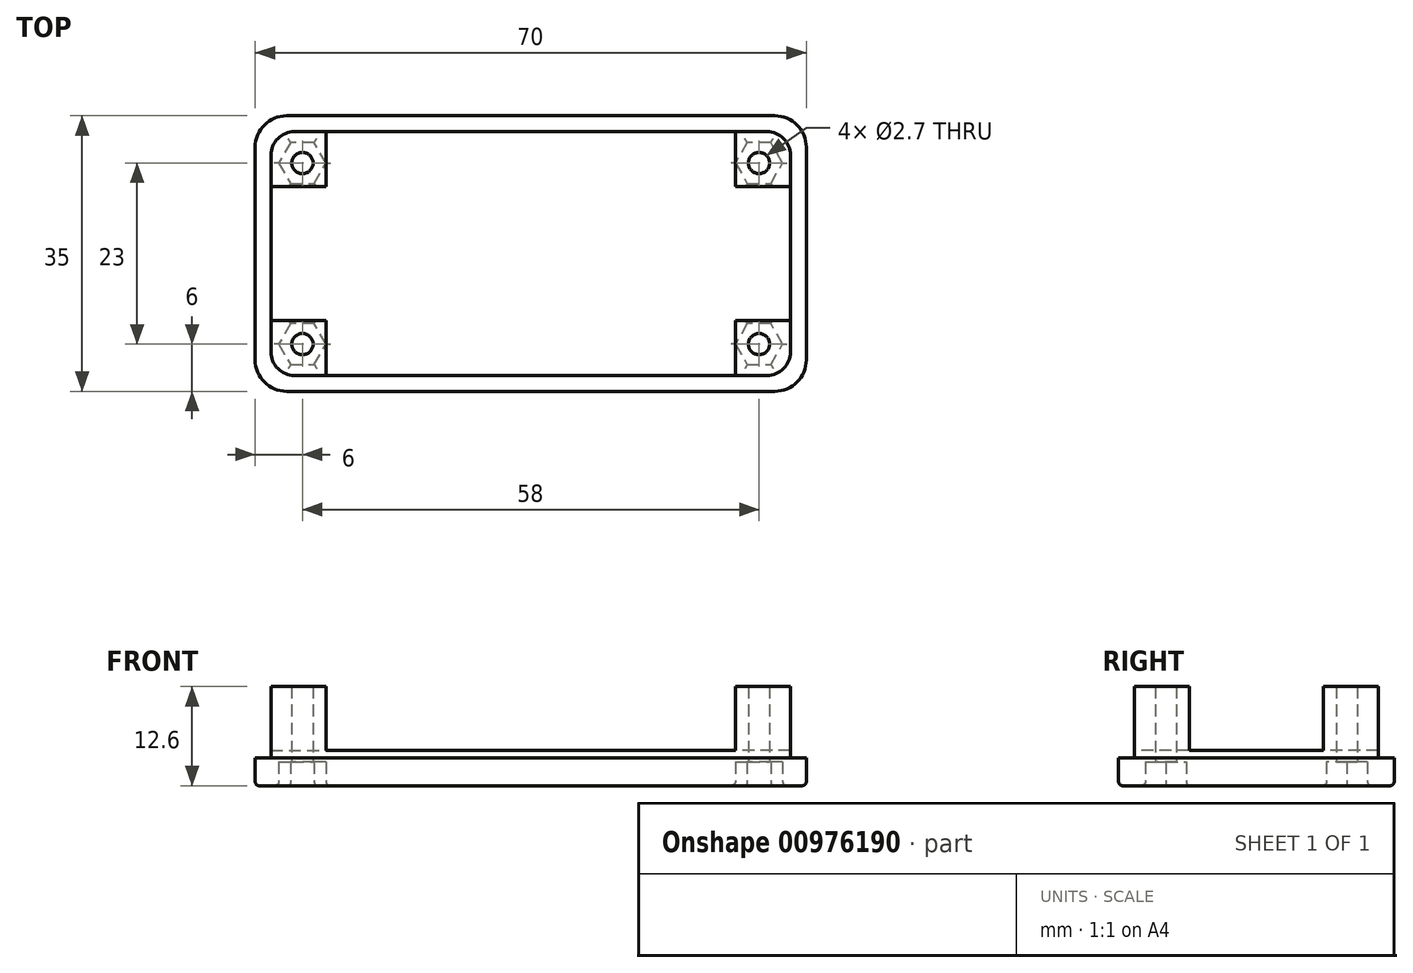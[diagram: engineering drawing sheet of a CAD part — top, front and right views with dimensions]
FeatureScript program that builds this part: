
annotation { "Feature Type Name" : "Feature", "Feature Type Description" : "" }
export const myFeature = defineFeature(function(context is Context, id is Id, definition is map)
    precondition{}
    {
        {
            var Q0;
            Q0=qCreatedBy(makeId("Top.planeOp"),FACE);
            var sketch = newSketch(context, id + "F0", { "sketchPlane" : qUnion([Q0])});
            skLineSegment(sketch, "E0.bottom", {"start": v(-31, 17.5) * mm, "end": v(31, 17.5) * mm});
            skLineSegment(sketch, "E0.top", {"start": v(-31, -17.5) * mm, "end": v(31, -17.5) * mm});
            skLineSegment(sketch, "E0.left", {"start": v(-35, 13.5) * mm, "end": v(-35, -13.5) * mm});
            skLineSegment(sketch, "E0.right", {"start": v(35, 13.5) * mm, "end": v(35, -13.5) * mm});
            skPoint(sketch, "E1.visualSharp", {"position": v(-35, 17.5) * mm});
            skArc(sketch, "E1.filletArc", {"start": v(-31, 17.5) * mm, "mid": v(-33.83, 16.33) * mm, "end": v(-35, 13.5) * mm});
            skPoint(sketch, "E2.visualSharp", {"position": v(-35, -17.5) * mm});
            skArc(sketch, "E2.filletArc", {"start": v(-35, -13.5) * mm, "mid": v(-33.83, -16.33) * mm, "end": v(-31, -17.5) * mm});
            skPoint(sketch, "E3.visualSharp", {"position": v(35, -17.5) * mm});
            skArc(sketch, "E3.filletArc", {"start": v(31, -17.5) * mm, "mid": v(33.83, -16.33) * mm, "end": v(35, -13.5) * mm});
            skPoint(sketch, "E4.visualSharp", {"position": v(35, 17.5) * mm});
            skArc(sketch, "E4.filletArc", {"start": v(35, 13.5) * mm, "mid": v(33.83, 16.33) * mm, "end": v(31, 17.5) * mm});
            skSolve(sketch);
        }
        {
            var Q0;
            Q0=makeQuery(id+"F0.imprint","IMPRINT",FACE,{"disambiguationData":[TD([[makeQuery(id+"F0.imprint","IMPRINT",EDGE,{"derivedFrom":sQuery(id+"F0.wireOp",EDGE,"E0.bottom")}),-1.0]])]});
            extrude(context, id + "F1", {"entities" : qUnion([Q0]), "depth" : 3.5 * mm, "offsetDistance" : 25 * mm});
        }
        {
            var Q0;
            Q0=makeQuery(id+"F1.opExtrude","CAP_FACE",FACE,{"disambiguationData":[OSD([sQuery(id+"F0.wireOp",EDGE,"E0.bottom"),sQuery(id+"F0.wireOp",EDGE,"E0.top"),sQuery(id+"F0.wireOp",EDGE,"E0.left"),sQuery(id+"F0.wireOp",EDGE,"E0.right"),sQuery(id+"F0.wireOp",EDGE,"E1.filletArc"),sQuery(id+"F0.wireOp",EDGE,"E2.filletArc"),sQuery(id+"F0.wireOp",EDGE,"E3.filletArc"),sQuery(id+"F0.wireOp",EDGE,"E4.filletArc")])],"isStart":false});
            var sketch = newSketch(context, id + "F2", { "sketchPlane" : qUnion([Q0])});
            skLineSegment(sketch, "E5.bottom", {"start": v(-30, 15.5) * mm, "end": v(30, 15.5) * mm});
            skLineSegment(sketch, "E5.top", {"start": v(-30, -15.5) * mm, "end": v(30, -15.5) * mm});
            skLineSegment(sketch, "E5.left", {"start": v(-33, 12.5) * mm, "end": v(-33, -12.5) * mm});
            skLineSegment(sketch, "E5.right", {"start": v(33, 12.5) * mm, "end": v(33, -12.5) * mm});
            skPoint(sketch, "E6.visualSharp", {"position": v(-33, 15.5) * mm});
            skArc(sketch, "E6.filletArc", {"start": v(-30, 15.5) * mm, "mid": v(-32.12, 14.62) * mm, "end": v(-33, 12.5) * mm});
            skPoint(sketch, "E7.visualSharp", {"position": v(-33, -15.5) * mm});
            skArc(sketch, "E7.filletArc", {"start": v(-33, -12.5) * mm, "mid": v(-32.12, -14.62) * mm, "end": v(-30, -15.5) * mm});
            skPoint(sketch, "E8.visualSharp", {"position": v(33, -15.5) * mm});
            skArc(sketch, "E8.filletArc", {"start": v(30, -15.5) * mm, "mid": v(32.12, -14.62) * mm, "end": v(33, -12.5) * mm});
            skPoint(sketch, "E9.visualSharp", {"position": v(33, 15.5) * mm});
            skArc(sketch, "E9.filletArc", {"start": v(33, 12.5) * mm, "mid": v(32.12, 14.62) * mm, "end": v(30, 15.5) * mm});
            skSolve(sketch);
        }
        {
            var Q0;
            Q0=qSketchRegion(id+"F2",true);
            extrude(context, id + "F3", {"entities" : qUnion([Q0]), "operationType" : NewBodyOperationType.ADD, "depth" : 1 * mm, "offsetDistance" : 25 * mm});
        }
        {
            var Q0;
            Q0=makeQuery(id+"F3.opExtrude","CAP_FACE",FACE,{"disambiguationData":[OSD([sQuery(id+"F2.wireOp",EDGE,"E5.bottom"),sQuery(id+"F2.wireOp",EDGE,"E5.top"),sQuery(id+"F2.wireOp",EDGE,"E5.left"),sQuery(id+"F2.wireOp",EDGE,"E5.right"),sQuery(id+"F2.wireOp",EDGE,"E6.filletArc"),sQuery(id+"F2.wireOp",EDGE,"E7.filletArc"),sQuery(id+"F2.wireOp",EDGE,"E8.filletArc"),sQuery(id+"F2.wireOp",EDGE,"E9.filletArc")])],"isStart":false});
            var sketch = newSketch(context, id + "F4", { "sketchPlane" : qUnion([Q0])});
            skLineSegment(sketch, "E10.bottom", {"start": v(-30, 15.5) * mm, "end": v(-26, 15.5) * mm});
            skLineSegment(sketch, "E10.top", {"start": v(-33, 8.5) * mm, "end": v(-26, 8.5) * mm});
            skLineSegment(sketch, "E10.left", {"start": v(-33, 12.5) * mm, "end": v(-33, 8.5) * mm});
            skLineSegment(sketch, "E10.right", {"start": v(-26, 15.5) * mm, "end": v(-26, 8.5) * mm});
            skLineSegment(sketch, "E11.bottom", {"start": v(-33, -8.5) * mm, "end": v(-26, -8.5) * mm});
            skLineSegment(sketch, "E11.top", {"start": v(-30, -15.5) * mm, "end": v(-26, -15.5) * mm});
            skLineSegment(sketch, "E11.left", {"start": v(-33, -8.5) * mm, "end": v(-33, -12.5) * mm});
            skLineSegment(sketch, "E11.right", {"start": v(-26, -8.5) * mm, "end": v(-26, -15.5) * mm});
            skLineSegment(sketch, "E12.bottom", {"start": v(26, 15.5) * mm, "end": v(30, 15.5) * mm});
            skLineSegment(sketch, "E12.top", {"start": v(26, 8.5) * mm, "end": v(33, 8.5) * mm});
            skLineSegment(sketch, "E12.left", {"start": v(26, 15.5) * mm, "end": v(26, 8.5) * mm});
            skLineSegment(sketch, "E12.right", {"start": v(33, 12.5) * mm, "end": v(33, 8.5) * mm});
            skLineSegment(sketch, "E13.bottom", {"start": v(33, -8.5) * mm, "end": v(26, -8.5) * mm});
            skLineSegment(sketch, "E13.top", {"start": v(30, -15.5) * mm, "end": v(26, -15.5) * mm});
            skLineSegment(sketch, "E13.left", {"start": v(33, -8.5) * mm, "end": v(33, -12.5) * mm});
            skLineSegment(sketch, "E13.right", {"start": v(26, -8.5) * mm, "end": v(26, -15.5) * mm});
            skPoint(sketch, "E14.visualSharp", {"position": v(-33, 15.5) * mm});
            skArc(sketch, "E14.filletArc", {"start": v(-30, 15.5) * mm, "mid": v(-32.12, 14.62) * mm, "end": v(-33, 12.5) * mm});
            skPoint(sketch, "E15.visualSharp", {"position": v(-33, -15.5) * mm});
            skArc(sketch, "E15.filletArc", {"start": v(-33, -12.5) * mm, "mid": v(-32.12, -14.62) * mm, "end": v(-30, -15.5) * mm});
            skPoint(sketch, "E16.visualSharp", {"position": v(33, -15.5) * mm});
            skArc(sketch, "E16.filletArc", {"start": v(30, -15.5) * mm, "mid": v(32.12, -14.62) * mm, "end": v(33, -12.5) * mm});
            skPoint(sketch, "E17.visualSharp", {"position": v(33, 15.5) * mm});
            skArc(sketch, "E17.filletArc", {"start": v(33, 12.5) * mm, "mid": v(32.12, 14.62) * mm, "end": v(30, 15.5) * mm});
            skSolve(sketch);
        }
        {
            var Q0;
            Q0=qSketchRegion(id+"F4",true);
            extrude(context, id + "F5", {"entities" : qUnion([Q0]), "operationType" : NewBodyOperationType.ADD, "depth" : 8.1 * mm, "offsetDistance" : 25 * mm});
        }
        {
            var Q0;
            Q0=makeQuery(id+"F1.opExtrude","CAP_FACE",FACE,{"disambiguationData":[OSD([sQuery(id+"F0.wireOp",EDGE,"E0.bottom"),sQuery(id+"F0.wireOp",EDGE,"E0.top"),sQuery(id+"F0.wireOp",EDGE,"E0.left"),sQuery(id+"F0.wireOp",EDGE,"E0.right"),sQuery(id+"F0.wireOp",EDGE,"E1.filletArc"),sQuery(id+"F0.wireOp",EDGE,"E2.filletArc"),sQuery(id+"F0.wireOp",EDGE,"E3.filletArc"),sQuery(id+"F0.wireOp",EDGE,"E4.filletArc")])],"isStart":true});
            var sketch = newSketch(context, id + "F6", { "sketchPlane" : qUnion([Q0])});
            skPoint(sketch, "E18", {"position": v(-29, 11.5) * mm});
            skPoint(sketch, "E19", {"position": v(-29, -11.5) * mm});
            skPoint(sketch, "E20", {"position": v(29, -11.5) * mm});
            skPoint(sketch, "E21", {"position": v(29, 11.5) * mm});
            skCircle(sketch, "E22.cCircle", {"center": v(-29, 11.5) * mm, "radius": 2.6 * mm, "construction": true});
            skLineSegment(sketch, "E22.0", {"start": v(-27.5, 8.9) * mm, "end": v(-30.5, 8.9) * mm});
            skLineSegment(sketch, "E22.1", {"start": v(-30.5, 8.9) * mm, "end": v(-32, 11.5) * mm});
            skLineSegment(sketch, "E22.2", {"start": v(-32, 11.5) * mm, "end": v(-30.5, 14.1) * mm});
            skLineSegment(sketch, "E22.3", {"start": v(-30.5, 14.1) * mm, "end": v(-27.5, 14.1) * mm});
            skLineSegment(sketch, "E22.4", {"start": v(-27.5, 14.1) * mm, "end": v(-26, 11.5) * mm});
            skLineSegment(sketch, "E22.5", {"start": v(-26, 11.5) * mm, "end": v(-27.5, 8.9) * mm});
            skPoint(sketch, "E22.0.midPoint", {"position": v(-29, 8.9) * mm});
            skCircle(sketch, "E23.cCircle", {"center": v(29, 11.5) * mm, "radius": 2.6 * mm, "construction": true});
            skLineSegment(sketch, "E23.0", {"start": v(30.5, 8.9) * mm, "end": v(27.5, 8.9) * mm});
            skLineSegment(sketch, "E23.1", {"start": v(27.5, 8.9) * mm, "end": v(26, 11.5) * mm});
            skLineSegment(sketch, "E23.2", {"start": v(26, 11.5) * mm, "end": v(27.5, 14.1) * mm});
            skLineSegment(sketch, "E23.3", {"start": v(27.5, 14.1) * mm, "end": v(30.5, 14.1) * mm});
            skLineSegment(sketch, "E23.4", {"start": v(30.5, 14.1) * mm, "end": v(32, 11.5) * mm});
            skLineSegment(sketch, "E23.5", {"start": v(32, 11.5) * mm, "end": v(30.5, 8.9) * mm});
            skPoint(sketch, "E23.0.midPoint", {"position": v(29, 8.9) * mm});
            skCircle(sketch, "E24.cCircle", {"center": v(29, -11.5) * mm, "radius": 2.6 * mm, "construction": true});
            skLineSegment(sketch, "E24.0", {"start": v(27.5, -8.9) * mm, "end": v(30.5, -8.9) * mm});
            skLineSegment(sketch, "E24.1", {"start": v(30.5, -8.9) * mm, "end": v(32, -11.5) * mm});
            skLineSegment(sketch, "E24.2", {"start": v(32, -11.5) * mm, "end": v(30.5, -14.1) * mm});
            skLineSegment(sketch, "E24.3", {"start": v(30.5, -14.1) * mm, "end": v(27.5, -14.1) * mm});
            skLineSegment(sketch, "E24.4", {"start": v(27.5, -14.1) * mm, "end": v(26, -11.5) * mm});
            skLineSegment(sketch, "E24.5", {"start": v(26, -11.5) * mm, "end": v(27.5, -8.9) * mm});
            skPoint(sketch, "E24.0.midPoint", {"position": v(29, -8.9) * mm});
            skCircle(sketch, "E25.cCircle", {"center": v(-29, -11.5) * mm, "radius": 2.6 * mm, "construction": true});
            skLineSegment(sketch, "E25.0", {"start": v(-30.5, -8.9) * mm, "end": v(-27.5, -8.9) * mm});
            skLineSegment(sketch, "E25.1", {"start": v(-27.5, -8.9) * mm, "end": v(-26, -11.5) * mm});
            skLineSegment(sketch, "E25.2", {"start": v(-26, -11.5) * mm, "end": v(-27.5, -14.1) * mm});
            skLineSegment(sketch, "E25.3", {"start": v(-27.5, -14.1) * mm, "end": v(-30.5, -14.1) * mm});
            skLineSegment(sketch, "E25.4", {"start": v(-30.5, -14.1) * mm, "end": v(-32, -11.5) * mm});
            skLineSegment(sketch, "E25.5", {"start": v(-32, -11.5) * mm, "end": v(-30.5, -8.9) * mm});
            skPoint(sketch, "E25.0.midPoint", {"position": v(-29, -8.9) * mm});
            skCircle(sketch, "E26", {"center": v(-29, 11.5) * mm, "radius": 1.35 * mm});
            skCircle(sketch, "E27", {"center": v(29, 11.5) * mm, "radius": 1.35 * mm});
            skCircle(sketch, "E28", {"center": v(29, -11.5) * mm, "radius": 1.35 * mm});
            skCircle(sketch, "E29", {"center": v(-29, -11.5) * mm, "radius": 1.35 * mm});
            skSolve(sketch);
        }
        {
            var Q0;
            Q0=qSketchRegion(id+"F6",true);
            extrude(context, id + "F7", {"entities" : qUnion([Q0]), "operationType" : NewBodyOperationType.REMOVE, "oppositeDirection" : true, "depth" : 3 * mm, "offsetDistance" : 25 * mm});
        }
        {
            var Q0;
            Q0=makeQuery(id+"F7.boolean.opBoolean","SPLIT",FACE,{"disambiguationData":[TD([makeQuery(id+"F7.opExtrude","SWEPT_FACE",FACE,{"disambiguationData":[OSD([sQuery(id+"F6.wireOp",EDGE,"E26")])]})])],"derivedFrom":makeQuery(id+"F1.opExtrude","CAP_FACE",FACE,{"disambiguationData":[OSD([sQuery(id+"F0.wireOp",EDGE,"E0.bottom"),sQuery(id+"F0.wireOp",EDGE,"E0.top"),sQuery(id+"F0.wireOp",EDGE,"E0.left"),sQuery(id+"F0.wireOp",EDGE,"E0.right"),sQuery(id+"F0.wireOp",EDGE,"E1.filletArc"),sQuery(id+"F0.wireOp",EDGE,"E2.filletArc"),sQuery(id+"F0.wireOp",EDGE,"E3.filletArc"),sQuery(id+"F0.wireOp",EDGE,"E4.filletArc")])],"isStart":true})});
            var Q1;
            Q1=makeQuery(id+"F7.boolean.opBoolean","SPLIT",FACE,{"disambiguationData":[TD([makeQuery(id+"F7.opExtrude","SWEPT_FACE",FACE,{"disambiguationData":[OSD([sQuery(id+"F6.wireOp",EDGE,"E27")])]})])],"derivedFrom":makeQuery(id+"F1.opExtrude","CAP_FACE",FACE,{"disambiguationData":[OSD([sQuery(id+"F0.wireOp",EDGE,"E0.bottom"),sQuery(id+"F0.wireOp",EDGE,"E0.top"),sQuery(id+"F0.wireOp",EDGE,"E0.left"),sQuery(id+"F0.wireOp",EDGE,"E0.right"),sQuery(id+"F0.wireOp",EDGE,"E1.filletArc"),sQuery(id+"F0.wireOp",EDGE,"E2.filletArc"),sQuery(id+"F0.wireOp",EDGE,"E3.filletArc"),sQuery(id+"F0.wireOp",EDGE,"E4.filletArc")])],"isStart":true})});
            var Q2;
            Q2=makeQuery(id+"F7.boolean.opBoolean","SPLIT",FACE,{"disambiguationData":[TD([makeQuery(id+"F7.opExtrude","SWEPT_FACE",FACE,{"disambiguationData":[OSD([sQuery(id+"F6.wireOp",EDGE,"E28")])]})])],"derivedFrom":makeQuery(id+"F1.opExtrude","CAP_FACE",FACE,{"disambiguationData":[OSD([sQuery(id+"F0.wireOp",EDGE,"E0.bottom"),sQuery(id+"F0.wireOp",EDGE,"E0.top"),sQuery(id+"F0.wireOp",EDGE,"E0.left"),sQuery(id+"F0.wireOp",EDGE,"E0.right"),sQuery(id+"F0.wireOp",EDGE,"E1.filletArc"),sQuery(id+"F0.wireOp",EDGE,"E2.filletArc"),sQuery(id+"F0.wireOp",EDGE,"E3.filletArc"),sQuery(id+"F0.wireOp",EDGE,"E4.filletArc")])],"isStart":true})});
            var Q3;
            Q3=makeQuery(id+"F7.boolean.opBoolean","SPLIT",FACE,{"disambiguationData":[TD([makeQuery(id+"F7.opExtrude","SWEPT_FACE",FACE,{"disambiguationData":[OSD([sQuery(id+"F6.wireOp",EDGE,"E29")])]})])],"derivedFrom":makeQuery(id+"F1.opExtrude","CAP_FACE",FACE,{"disambiguationData":[OSD([sQuery(id+"F0.wireOp",EDGE,"E0.bottom"),sQuery(id+"F0.wireOp",EDGE,"E0.top"),sQuery(id+"F0.wireOp",EDGE,"E0.left"),sQuery(id+"F0.wireOp",EDGE,"E0.right"),sQuery(id+"F0.wireOp",EDGE,"E1.filletArc"),sQuery(id+"F0.wireOp",EDGE,"E2.filletArc"),sQuery(id+"F0.wireOp",EDGE,"E3.filletArc"),sQuery(id+"F0.wireOp",EDGE,"E4.filletArc")])],"isStart":true})});
            extrude(context, id + "F8", {"entities" : qUnion([Q0, Q1, Q2, Q3]), "operationType" : NewBodyOperationType.REMOVE, "endBound" : BoundingType.THROUGH_ALL, "oppositeDirection" : true, "depth" : 25 * mm, "offsetDistance" : 25 * mm});
        }
        {
            var Q0;
            {var subQ0=sQuery(id+"F0.wireOp",EDGE,"E3.filletArc");var subQ1=sQuery(id+"F0.wireOp",EDGE,"E2.filletArc");var subQ2=sQuery(id+"F0.wireOp",EDGE,"E1.filletArc");var subQ3=sQuery(id+"F0.wireOp",EDGE,"E0.right");var subQ4=sQuery(id+"F0.wireOp",EDGE,"E0.left");var subQ5=sQuery(id+"F0.wireOp",EDGE,"E0.bottom");var subQ6=sQuery(id+"F0.wireOp",EDGE,"E0.top");var subQ7=sQuery(id+"F0.wireOp",EDGE,"E4.filletArc");Q0=makeQuery(id+"F7.boolean.opBoolean","SPLIT",FACE,{"disambiguationData":[TD([makeQuery(id+"F1.opExtrude","SWEPT_FACE",FACE,{"disambiguationData":[OSD([subQ5])]})])],"derivedFrom":makeQuery(id+"F1.opExtrude","CAP_FACE",FACE,{"disambiguationData":[OSD([subQ5,subQ6,subQ4,subQ3,subQ2,subQ1,subQ0,subQ7])],"isStart":true})});}
            fillet(context, id + "F9", {"entities" : qUnion([Q0]), "radius" : .5 * mm, "tangentPropagation" : true, "allowEdgeOverflow" : false});
        }
    });
